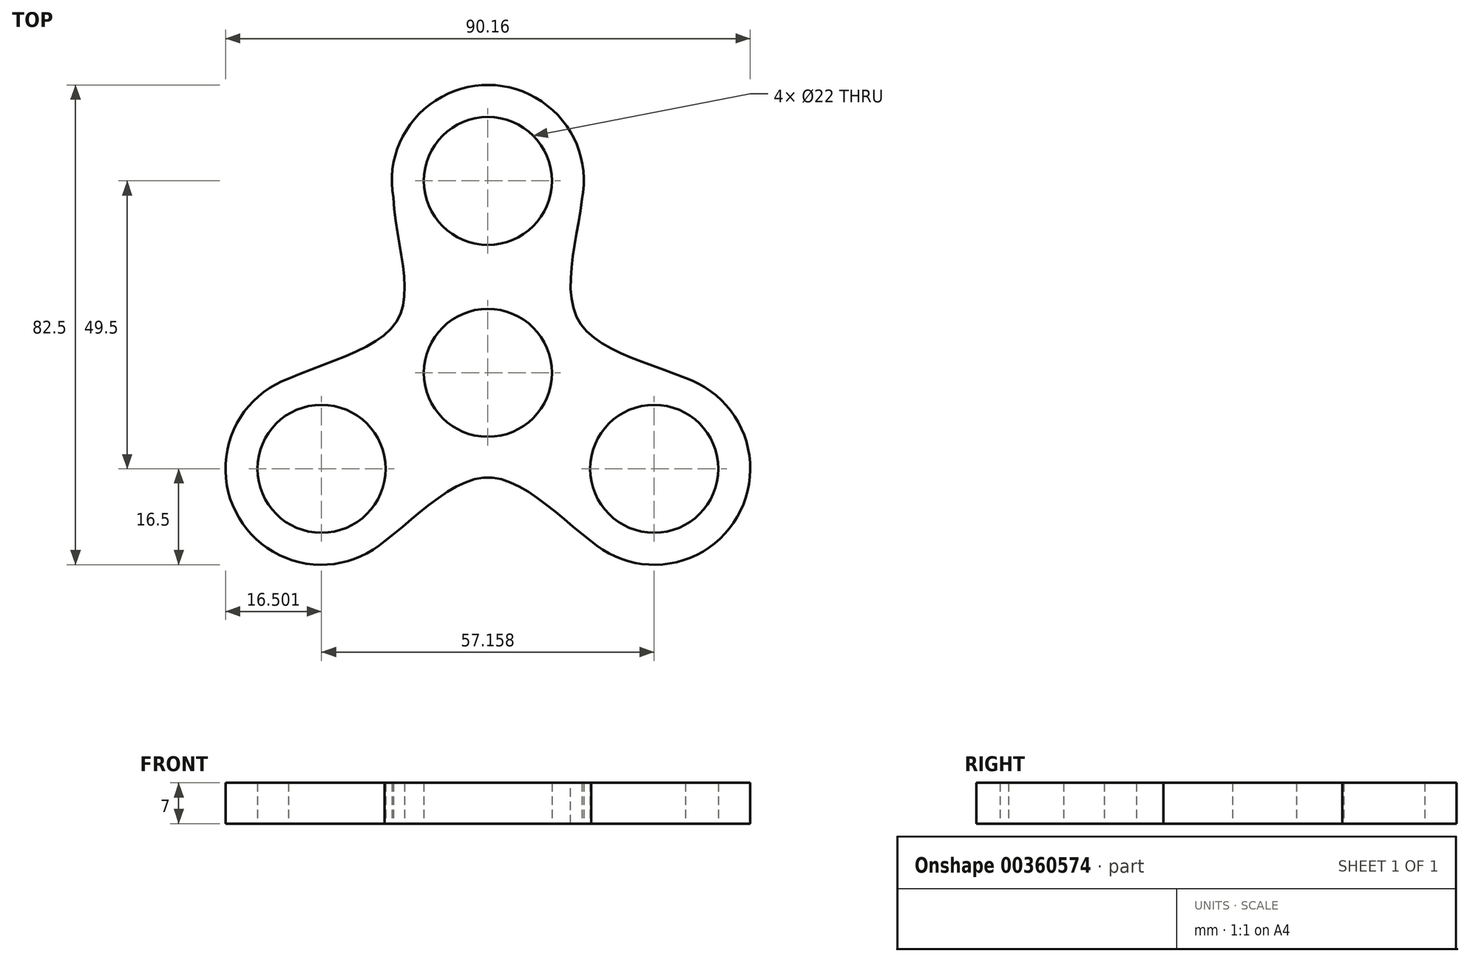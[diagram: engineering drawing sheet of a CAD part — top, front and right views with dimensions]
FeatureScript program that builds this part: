
annotation { "Feature Type Name" : "Feature", "Feature Type Description" : "" }
export const myFeature = defineFeature(function(context is Context, id is Id, definition is map)
    precondition{}
    {
        {
            var Q0;
            Q0=qCreatedBy(makeId("Top.planeOp"),FACE);
            var sketch = newSketch(context, id + "F0", { "sketchPlane" : qUnion([Q0])});
            skCircle(sketch, "E0", {"center": v(0, 0) * mm, "radius": 11 * mm});
            skCircle(sketch, "E1", {"center": v(0, 33) * mm, "radius": 11 * mm});
            skCircle(sketch, "E2", {"center": v(28.58, -16.5) * mm, "radius": 11 * mm});
            skCircle(sketch, "E3", {"center": v(-28.58, -16.5) * mm, "radius": 11 * mm});
            skCircle(sketch, "E4.0", {"center": v(0, 0) * mm, "radius": 16.5 * mm});
            skCircle(sketch, "E5.0", {"center": v(0, 33) * mm, "radius": 16.5 * mm});
            skCircle(sketch, "E6.0", {"center": v(-28.58, -16.5) * mm, "radius": 16.5 * mm});
            skCircle(sketch, "E7.0", {"center": v(28.58, -16.5) * mm, "radius": 16.5 * mm});
            skFitSpline(sketch, "E8", {"points": [v(-16.25, 30.13) * mm, v(-15.59, 9) * mm, v(-36.83, -2.21) * mm], "startDerivative": vector(2.5, -48.4) * mm, "endDerivative": vector(-43.16, -22.03) * mm});
            skFitSpline(sketch, "E9", {"points": [v(-20.33, -30.79) * mm, v(0, -18) * mm, v(20.33, -30.79) * mm], "startDerivative": vector(40.66, 26.37) * mm, "endDerivative": vector(40.66, -26.37) * mm});
            skFitSpline(sketch, "E10", {"points": [v(16.5, 33) * mm, v(15.59, 9) * mm, v(36.83, -2.21) * mm], "startDerivative": vector(-2.5, -48.4) * mm, "endDerivative": vector(43.16, -22.03) * mm});
            skLineSegment(sketch, "E11", {"start": v(0, 33) * mm, "end": v(-14.29, 24.75) * mm});
            skLineSegment(sketch, "E12", {"start": v(0, 33) * mm, "end": v(-16.25, 30.13) * mm});
            skSolve(sketch);
        }
        {
            var Q0;
            Q0 = qSketchRegion(id + "F0", true);
            var Q1;
            Q1=makeQuery(id+"F0.imprint","IMPRINT",FACE,{"disambiguationData":[TD([[makeQuery(id+"F0.imprint","IMPRINT",EDGE,{"derivedFrom":sQuery(id+"F0.wireOp",EDGE,"E0")}),-1.0]])]});
            extrude(context, id + "F1", {"entities" : qUnion([Q0, Q1]), "endBound" : BoundingType.SYMMETRIC, "depth" : 7 * mm});
        }
    });
